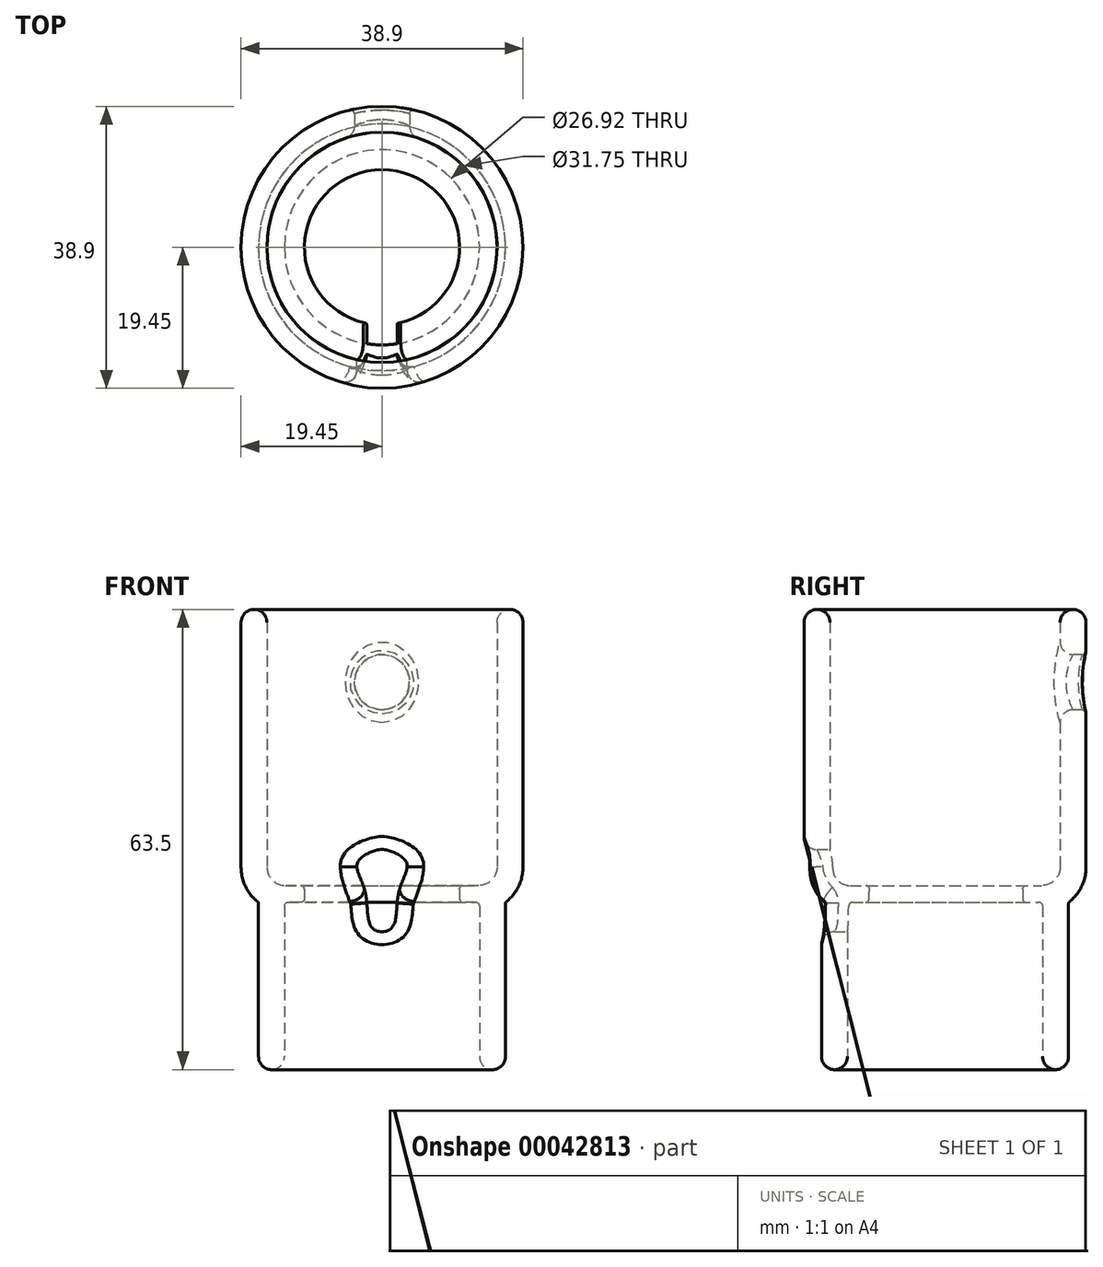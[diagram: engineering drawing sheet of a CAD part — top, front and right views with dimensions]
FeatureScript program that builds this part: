
annotation { "Feature Type Name" : "Feature", "Feature Type Description" : "" }
export const myFeature = defineFeature(function(context is Context, id is Id, definition is map)
    precondition{}
    {
        {
            var Q0;
            Q0=qCreatedBy(makeId("Front.planeOp"),FACE);
            var sketch = newSketch(context, id + "F0", { "sketchPlane" : qUnion([Q0])});
            skLineSegment(sketch, "E0", {"start": v(15.87, 61.71) * mm, "end": v(15.87, 27.94) * mm});
            skLineSegment(sketch, "E1", {"start": v(13.33, 25.4) * mm, "end": v(11.21, 25.4) * mm});
            skLineSegment(sketch, "E2", {"start": v(13.46, 22.57) * mm, "end": v(13.46, 1.79) * mm});
            skPoint(sketch, "E3.visualSharp", {"position": v(15.88, 25.4) * mm});
            skArc(sketch, "E3.filletArc", {"start": v(13.33, 25.4) * mm, "mid": v(15.13, 26.14) * mm, "end": v(15.87, 27.94) * mm});
            skLineSegment(sketch, "E4", {"start": v(0, -28.34) * mm, "end": v(0, 90.61) * mm, "construction": true});
            skCircle(sketch, "E5", {"center": v(0, 53.46) * mm, "radius": 3.81 * mm});
            skPoint(sketch, "E6", {"position": v(0, 61.71) * mm});
            skLineSegment(sketch, "E7.0", {"start": v(17.03, 22.83) * mm, "end": v(17.03, 1.79) * mm});
            skArc(sketch, "E7.1", {"start": v(17.22, 23.22) * mm, "mid": v(18.86, 25.33) * mm, "end": v(19.45, 27.94) * mm});
            skLineSegment(sketch, "E7.2", {"start": v(19.45, 61.71) * mm, "end": v(19.45, 27.94) * mm});
            skArc(sketch, "E8", {"start": v(15.87, 61.71) * mm, "mid": v(17.66, 63.5) * mm, "end": v(19.45, 61.71) * mm});
            skArc(sketch, "E9", {"start": v(13.46, 1.79) * mm, "mid": v(15.25, 0) * mm, "end": v(17.03, 1.79) * mm});
            skPoint(sketch, "E10", {"position": v(15.25, 0) * mm});
            skPoint(sketch, "E11", {"position": v(17.66, 63.5) * mm});
            skLineSegment(sketch, "E12", {"start": v(10.7, 24.9) * mm, "end": v(10.7, 23.58) * mm});
            skLineSegment(sketch, "E13", {"start": v(11.21, 23.07) * mm, "end": v(12.95, 23.07) * mm});
            skPoint(sketch, "E14.visualSharp", {"position": v(10.7, 25.4) * mm});
            skArc(sketch, "E14.filletArc", {"start": v(11.21, 25.4) * mm, "mid": v(10.85, 25.25) * mm, "end": v(10.7, 24.9) * mm});
            skPoint(sketch, "E15.visualSharp", {"position": v(10.7, 23.07) * mm});
            skArc(sketch, "E15.filletArc", {"start": v(10.7, 23.58) * mm, "mid": v(10.85, 23.22) * mm, "end": v(11.21, 23.07) * mm});
            skPoint(sketch, "E16.visualSharp", {"position": v(13.46, 23.07) * mm});
            skArc(sketch, "E16.filletArc", {"start": v(13.46, 22.57) * mm, "mid": v(13.31, 22.93) * mm, "end": v(12.95, 23.07) * mm});
            skPoint(sketch, "E17.visualSharp", {"position": v(17.03, 23.07) * mm});
            skArc(sketch, "E17.filletArc", {"start": v(17.22, 23.22) * mm, "mid": v(17.08, 23.05) * mm, "end": v(17.03, 22.83) * mm});
            skSolve(sketch);
        }
        {
            var Q0;
            Q0=makeQuery(id+"F0.imprint","IMPRINT",FACE,{"disambiguationData":[TD([[makeQuery(id+"F0.imprint","IMPRINT",EDGE,{"derivedFrom":sQuery(id+"F0.wireOp",EDGE,"E0")}),1.0]])]});
            var Q1;
            Q1=sQuery(id+"F0.wireOp",EDGE,"E4");
            revolve(context, id + "F1", {"entities" : qUnion([Q0]), "axis" : qUnion([Q1]), "revolveType" : RevolveType.FULL});
        }
        {
            var Q0;
            Q0=makeQuery(id+"F0.imprint","IMPRINT",FACE,{"disambiguationData":[TD([[makeQuery(id+"F0.imprint","IMPRINT",EDGE,{"derivedFrom":sQuery(id+"F0.wireOp",EDGE,"E5")}),1.0]])]});
            extrude(context, id + "F2", {"entities" : qUnion([Q0]), "operationType" : NewBodyOperationType.REMOVE, "oppositeDirection" : true, "depth" : 38.1 * mm});
        }
        {
            var Q0;
            Q0=makeQuery(id+"F2.boolean.opBoolean","INTERSECT",EDGE,{"derivedFrom":[makeQuery(id+"F1.opRevolve","SWEPT_FACE",FACE,{"disambiguationData":[OSD([sQuery(id+"F0.wireOp",EDGE,"E0")])]}),makeQuery(id+"F2.opExtrude","SWEPT_FACE",FACE,{"disambiguationData":[OSD([sQuery(id+"F0.wireOp",EDGE,"E5")])]})]});
            fillet(context, id + "F3", {"entities" : qUnion([Q0]), "radius" : 1.78 * mm, "tangentPropagation" : true, "allowEdgeOverflow" : false});
        }
        {
            var Q0;
            Q0=makeQuery(id+"F2.boolean.opBoolean","INTERSECT",EDGE,{"derivedFrom":[makeQuery(id+"F1.opRevolve","SWEPT_FACE",FACE,{"disambiguationData":[OSD([sQuery(id+"F0.wireOp",EDGE,"E7.2")])]}),makeQuery(id+"F2.opExtrude","SWEPT_FACE",FACE,{"disambiguationData":[OSD([sQuery(id+"F0.wireOp",EDGE,"E5")])]})]});
            fillet(context, id + "F4", {"entities" : qUnion([Q0]), "radius" : 0.5 * mm, "tangentPropagation" : true, "allowEdgeOverflow" : false});
        }
        {
            var Q0;
            Q0=qCreatedBy(makeId("Front.planeOp"),FACE);
            var sketch = newSketch(context, id + "F5", { "sketchPlane" : qUnion([Q0])});
            skFitSpline(sketch, "E18", {"points": [v(0, 19.02) * mm, v(2.24, 24.15) * mm, v(3.32, 28.68) * mm, v(0, 30.37) * mm], "startDerivative": vector(19.94, 0) * mm, "endDerivative": vector(-9.19, 0) * mm});
            skFitSpline(sketch, "E19.MirrorCS", {"points": [v(0, 19.02) * mm, v(-2.24, 24.15) * mm, v(-3.32, 28.68) * mm, v(0, 30.37) * mm], "startDerivative": vector(-19.94, 0) * mm, "endDerivative": vector(9.19, 0) * mm});
            skSolve(sketch);
        }
        {
            var Q0;
            Q0 = qSketchRegion(id + "F5", true);
            extrude(context, id + "F6", {"entities" : qUnion([Q0]), "depth" : 50.8 * mm});
        }
        {
            var Q0;
            Q0=makeQuery(id+"F6.opExtrude","SWEPT_BODY",BODY,{"disambiguationData":[OSD([sQuery(id+"F5.wireOp",EDGE,"E18"),sQuery(id+"F5.wireOp",EDGE,"E19.MirrorCS")])]});
            var Q1;
            Q1=makeQuery(id+"F1.opRevolve","SWEPT_BODY",BODY,{"disambiguationData":[OSD([sQuery(id+"F0.wireOp",EDGE,"E0"),sQuery(id+"F0.wireOp",EDGE,"E1"),sQuery(id+"F0.wireOp",EDGE,"E2"),sQuery(id+"F0.wireOp",EDGE,"665b7fc8-37b9-4214-9120-500ffdb07fa3.filletArc"),sQuery(id+"F0.wireOp",EDGE,"E3.filletArc"),sQuery(id+"F0.wireOp",EDGE,"E7.0"),sQuery(id+"F0.wireOp",EDGE,"E7.1"),sQuery(id+"F0.wireOp",EDGE,"E7.2"),sQuery(id+"F0.wireOp",EDGE,"E8"),sQuery(id+"F0.wireOp",EDGE,"E9")])]});
            booleanBodies(context, id + "F7", {"operationType" : BooleanOperationType.SUBTRACTION, "tools" : qUnion([Q0]), "targets" : qUnion([Q1])});
        }
        {
            var Q0;
            {var subQ0=sQuery(id+"F5.wireOp",EDGE,"E19.MirrorCS");var subQ1=sQuery(id+"F5.wireOp",EDGE,"E18");var subQ3=makeQuery(id+"F6.opExtrude","SWEPT_FACE",FACE,{"disambiguationData":[OSD([subQ1])]});var subQ4=makeQuery(id+"Fw3jHcx6r2MQuvf_2.opPattern","COPY",FACE,{"derivedFrom":subQ3,"instanceName":"1"});Q0=makeQuery(id+"F7.opBoolean","INTERSECT",EDGE,{"derivedFrom":[makeQuery(id+"F1.opRevolve","SWEPT_FACE",FACE,{"disambiguationData":[OSD([sQuery(id+"F0.wireOp",EDGE,"E7.1")])]}),makeQuery(id+"Fw3jHcx6r2MQuvf_2.boolean.opBoolean","SPLIT",FACE,{"disambiguationData":[TD([makeQuery(id+"Fw3jHcx6r2MQuvf_2.opPattern","COPY",FACE,{"derivedFrom":makeQuery(id+"F6.opExtrude","CAP_FACE",FACE,{"disambiguationData":[OSD([subQ1,subQ0])],"isStart":false}),"instanceName":"1"})])],"derivedFrom":subQ4})]});}
            var Q1;
            {var subQ0=sQuery(id+"F5.wireOp",EDGE,"E19.MirrorCS");var subQ1=sQuery(id+"F5.wireOp",EDGE,"E18");var subQ3=makeQuery(id+"F6.opExtrude","SWEPT_FACE",FACE,{"disambiguationData":[OSD([subQ1])]});var subQ4=makeQuery(id+"Fw3jHcx6r2MQuvf_2.opPattern","COPY",FACE,{"derivedFrom":subQ3,"instanceName":"1"});Q1=makeQuery(id+"F7.opBoolean","INTERSECT",EDGE,{"derivedFrom":[makeQuery(id+"F1.opRevolve","SWEPT_FACE",FACE,{"disambiguationData":[OSD([sQuery(id+"F0.wireOp",EDGE,"E7.0")])]}),makeQuery(id+"Fw3jHcx6r2MQuvf_2.boolean.opBoolean","SPLIT",FACE,{"disambiguationData":[TD([makeQuery(id+"Fw3jHcx6r2MQuvf_2.opPattern","COPY",FACE,{"derivedFrom":makeQuery(id+"F6.opExtrude","CAP_FACE",FACE,{"disambiguationData":[OSD([subQ1,subQ0])],"isStart":false}),"instanceName":"1"})])],"derivedFrom":subQ4})]});}
            var Q2;
            {var subQ0=sQuery(id+"F5.wireOp",EDGE,"E19.MirrorCS");var subQ1=sQuery(id+"F5.wireOp",EDGE,"E18");var subQ2=makeQuery(id+"F6.opExtrude","SWEPT_FACE",FACE,{"disambiguationData":[OSD([subQ0])]});var subQ4=makeQuery(id+"Fw3jHcx6r2MQuvf_2.opPattern","COPY",FACE,{"derivedFrom":subQ2,"instanceName":"1"});Q2=makeQuery(id+"F7.opBoolean","INTERSECT",EDGE,{"derivedFrom":[makeQuery(id+"F1.opRevolve","SWEPT_FACE",FACE,{"disambiguationData":[OSD([sQuery(id+"F0.wireOp",EDGE,"E7.0")])]}),makeQuery(id+"Fw3jHcx6r2MQuvf_2.boolean.opBoolean","SPLIT",FACE,{"disambiguationData":[TD([makeQuery(id+"Fw3jHcx6r2MQuvf_2.opPattern","COPY",FACE,{"derivedFrom":makeQuery(id+"F6.opExtrude","CAP_FACE",FACE,{"disambiguationData":[OSD([subQ1,subQ0])],"isStart":false}),"instanceName":"1"})])],"derivedFrom":subQ4})]});}
            var Q3;
            {var subQ0=sQuery(id+"F5.wireOp",EDGE,"E18");var subQ1=makeQuery(id+"F6.opExtrude","SWEPT_FACE",FACE,{"disambiguationData":[OSD([subQ0])]});var subQ2=sQuery(id+"F5.wireOp",EDGE,"E19.MirrorCS");Q3=makeQuery(id+"F7.opBoolean","INTERSECT",EDGE,{"derivedFrom":[makeQuery(id+"F1.opRevolve","SWEPT_FACE",FACE,{"disambiguationData":[OSD([sQuery(id+"F0.wireOp",EDGE,"E7.2")])]}),makeQuery(id+"Fw3jHcx6r2MQuvf_2.boolean.opBoolean","SPLIT",FACE,{"disambiguationData":[TD([makeQuery(id+"F6.opExtrude","CAP_FACE",FACE,{"disambiguationData":[OSD([subQ0,subQ2])],"isStart":false})])],"derivedFrom":subQ1})]});}
            var Q4;
            {var subQ0=sQuery(id+"F5.wireOp",EDGE,"E18");var subQ2=sQuery(id+"F5.wireOp",EDGE,"E19.MirrorCS");var subQ3=makeQuery(id+"F6.opExtrude","SWEPT_FACE",FACE,{"disambiguationData":[OSD([subQ2])]});Q4=makeQuery(id+"F7.opBoolean","INTERSECT",EDGE,{"derivedFrom":[makeQuery(id+"F1.opRevolve","SWEPT_FACE",FACE,{"disambiguationData":[OSD([sQuery(id+"F0.wireOp",EDGE,"E7.0")])]}),makeQuery(id+"Fw3jHcx6r2MQuvf_2.boolean.opBoolean","SPLIT",FACE,{"disambiguationData":[TD([makeQuery(id+"F6.opExtrude","CAP_FACE",FACE,{"disambiguationData":[OSD([subQ0,subQ2])],"isStart":false})])],"derivedFrom":subQ3})]});}
            var Q5;
            {var subQ0=sQuery(id+"F5.wireOp",EDGE,"E19.MirrorCS");var subQ2=sQuery(id+"F5.wireOp",EDGE,"E18");var subQ3=makeQuery(id+"F6.opExtrude","SWEPT_FACE",FACE,{"disambiguationData":[OSD([subQ2])]});var subQ4=makeQuery(id+"Fw3jHcx6r2MQuvf_2.opPattern","COPY",FACE,{"derivedFrom":subQ3,"instanceName":"2"});Q5=makeQuery(id+"F7.opBoolean","INTERSECT",EDGE,{"derivedFrom":[makeQuery(id+"F1.opRevolve","SWEPT_FACE",FACE,{"disambiguationData":[OSD([sQuery(id+"F0.wireOp",EDGE,"E7.0")])]}),makeQuery(id+"Fw3jHcx6r2MQuvf_2.boolean.opBoolean","SPLIT",FACE,{"disambiguationData":[TD([makeQuery(id+"Fw3jHcx6r2MQuvf_2.opPattern","COPY",FACE,{"derivedFrom":makeQuery(id+"F6.opExtrude","CAP_FACE",FACE,{"disambiguationData":[OSD([subQ2,subQ0])],"isStart":false}),"instanceName":"2"})])],"derivedFrom":subQ4})]});}
            var Q6;
            {var subQ0=sQuery(id+"F5.wireOp",EDGE,"E19.MirrorCS");var subQ2=sQuery(id+"F5.wireOp",EDGE,"E18");var subQ3=makeQuery(id+"F6.opExtrude","SWEPT_FACE",FACE,{"disambiguationData":[OSD([subQ2])]});var subQ4=makeQuery(id+"Fw3jHcx6r2MQuvf_2.opPattern","COPY",FACE,{"derivedFrom":subQ3,"instanceName":"2"});Q6=makeQuery(id+"F7.opBoolean","INTERSECT",EDGE,{"derivedFrom":[makeQuery(id+"F1.opRevolve","SWEPT_FACE",FACE,{"disambiguationData":[OSD([sQuery(id+"F0.wireOp",EDGE,"E7.1")])]}),makeQuery(id+"Fw3jHcx6r2MQuvf_2.boolean.opBoolean","SPLIT",FACE,{"disambiguationData":[TD([makeQuery(id+"Fw3jHcx6r2MQuvf_2.opPattern","COPY",FACE,{"derivedFrom":makeQuery(id+"F6.opExtrude","CAP_FACE",FACE,{"disambiguationData":[OSD([subQ2,subQ0])],"isStart":false}),"instanceName":"2"})])],"derivedFrom":subQ4})]});}
            var Q7;
            {var subQ0=sQuery(id+"F5.wireOp",EDGE,"E18");var subQ2=sQuery(id+"F5.wireOp",EDGE,"E19.MirrorCS");var subQ3=makeQuery(id+"F6.opExtrude","SWEPT_FACE",FACE,{"disambiguationData":[OSD([subQ2])]});Q7=makeQuery(id+"F7.opBoolean","INTERSECT",EDGE,{"derivedFrom":[makeQuery(id+"F1.opRevolve","SWEPT_FACE",FACE,{"disambiguationData":[OSD([sQuery(id+"F0.wireOp",EDGE,"E7.2")])]}),makeQuery(id+"Fw3jHcx6r2MQuvf_2.boolean.opBoolean","SPLIT",FACE,{"disambiguationData":[TD([makeQuery(id+"F6.opExtrude","CAP_FACE",FACE,{"disambiguationData":[OSD([subQ0,subQ2])],"isStart":true})])],"derivedFrom":subQ3})]});}
            var Q8;
            {var subQ0=sQuery(id+"F5.wireOp",EDGE,"E18");var subQ2=sQuery(id+"F5.wireOp",EDGE,"E19.MirrorCS");var subQ3=makeQuery(id+"F6.opExtrude","SWEPT_FACE",FACE,{"disambiguationData":[OSD([subQ2])]});Q8=makeQuery(id+"F7.opBoolean","INTERSECT",EDGE,{"derivedFrom":[makeQuery(id+"F1.opRevolve","SWEPT_FACE",FACE,{"disambiguationData":[OSD([sQuery(id+"F0.wireOp",EDGE,"E7.0")])]}),makeQuery(id+"Fw3jHcx6r2MQuvf_2.boolean.opBoolean","SPLIT",FACE,{"disambiguationData":[TD([makeQuery(id+"F6.opExtrude","CAP_FACE",FACE,{"disambiguationData":[OSD([subQ0,subQ2])],"isStart":true})])],"derivedFrom":subQ3})]});}
            var Q9;
            {var subQ0=sQuery(id+"F5.wireOp",EDGE,"E18");var subQ2=sQuery(id+"F5.wireOp",EDGE,"E19.MirrorCS");var subQ3=makeQuery(id+"F6.opExtrude","SWEPT_FACE",FACE,{"disambiguationData":[OSD([subQ2])]});Q9=makeQuery(id+"F7.opBoolean","INTERSECT",EDGE,{"derivedFrom":[makeQuery(id+"F1.opRevolve","SWEPT_FACE",FACE,{"disambiguationData":[OSD([sQuery(id+"F0.wireOp",EDGE,"E7.1")])]}),makeQuery(id+"Fw3jHcx6r2MQuvf_2.boolean.opBoolean","SPLIT",FACE,{"disambiguationData":[TD([makeQuery(id+"F6.opExtrude","CAP_FACE",FACE,{"disambiguationData":[OSD([subQ0,subQ2])],"isStart":true})])],"derivedFrom":subQ3})]});}
            var Q10;
            {var subQ0=sQuery(id+"F5.wireOp",EDGE,"E18");var subQ2=sQuery(id+"F5.wireOp",EDGE,"E19.MirrorCS");var subQ3=makeQuery(id+"F6.opExtrude","SWEPT_FACE",FACE,{"disambiguationData":[OSD([subQ2])]});var subQ4=makeQuery(id+"Fw3jHcx6r2MQuvf_2.opPattern","COPY",FACE,{"derivedFrom":subQ3,"instanceName":"1"});Q10=makeQuery(id+"F7.opBoolean","INTERSECT",EDGE,{"derivedFrom":[makeQuery(id+"F1.opRevolve","SWEPT_FACE",FACE,{"disambiguationData":[OSD([sQuery(id+"F0.wireOp",EDGE,"E7.1")])]}),makeQuery(id+"Fw3jHcx6r2MQuvf_2.boolean.opBoolean","SPLIT",FACE,{"disambiguationData":[TD([makeQuery(id+"Fw3jHcx6r2MQuvf_2.opPattern","COPY",FACE,{"derivedFrom":makeQuery(id+"F6.opExtrude","CAP_FACE",FACE,{"disambiguationData":[OSD([subQ0,subQ2])],"isStart":true}),"instanceName":"1"})])],"derivedFrom":subQ4})]});}
            var Q11;
            {var subQ0=sQuery(id+"F5.wireOp",EDGE,"E18");var subQ2=sQuery(id+"F5.wireOp",EDGE,"E19.MirrorCS");var subQ3=makeQuery(id+"F6.opExtrude","SWEPT_FACE",FACE,{"disambiguationData":[OSD([subQ2])]});var subQ4=makeQuery(id+"Fw3jHcx6r2MQuvf_2.opPattern","COPY",FACE,{"derivedFrom":subQ3,"instanceName":"1"});Q11=makeQuery(id+"F7.opBoolean","INTERSECT",EDGE,{"derivedFrom":[makeQuery(id+"F1.opRevolve","SWEPT_FACE",FACE,{"disambiguationData":[OSD([sQuery(id+"F0.wireOp",EDGE,"E7.2")])]}),makeQuery(id+"Fw3jHcx6r2MQuvf_2.boolean.opBoolean","SPLIT",FACE,{"disambiguationData":[TD([makeQuery(id+"Fw3jHcx6r2MQuvf_2.opPattern","COPY",FACE,{"derivedFrom":makeQuery(id+"F6.opExtrude","CAP_FACE",FACE,{"disambiguationData":[OSD([subQ0,subQ2])],"isStart":true}),"instanceName":"1"})])],"derivedFrom":subQ4})]});}
            var Q12;
            {var subQ0=sQuery(id+"F5.wireOp",EDGE,"E18");var subQ2=sQuery(id+"F5.wireOp",EDGE,"E19.MirrorCS");var subQ3=makeQuery(id+"F6.opExtrude","SWEPT_FACE",FACE,{"disambiguationData":[OSD([subQ2])]});var subQ4=makeQuery(id+"Fw3jHcx6r2MQuvf_2.opPattern","COPY",FACE,{"derivedFrom":subQ3,"instanceName":"1"});Q12=makeQuery(id+"F7.opBoolean","INTERSECT",EDGE,{"derivedFrom":[makeQuery(id+"F1.opRevolve","SWEPT_FACE",FACE,{"disambiguationData":[OSD([sQuery(id+"F0.wireOp",EDGE,"E7.0")])]}),makeQuery(id+"Fw3jHcx6r2MQuvf_2.boolean.opBoolean","SPLIT",FACE,{"disambiguationData":[TD([makeQuery(id+"Fw3jHcx6r2MQuvf_2.opPattern","COPY",FACE,{"derivedFrom":makeQuery(id+"F6.opExtrude","CAP_FACE",FACE,{"disambiguationData":[OSD([subQ0,subQ2])],"isStart":true}),"instanceName":"1"})])],"derivedFrom":subQ4})]});}
            var Q13;
            {var subQ0=sQuery(id+"F5.wireOp",EDGE,"E19.MirrorCS");var subQ1=makeQuery(id+"F6.opExtrude","SWEPT_FACE",FACE,{"disambiguationData":[OSD([subQ0])]});var subQ2=sQuery(id+"F5.wireOp",EDGE,"E18");var subQ4=makeQuery(id+"Fw3jHcx6r2MQuvf_2.opPattern","COPY",FACE,{"derivedFrom":subQ1,"instanceName":"2"});Q13=makeQuery(id+"F7.opBoolean","INTERSECT",EDGE,{"derivedFrom":[makeQuery(id+"F1.opRevolve","SWEPT_FACE",FACE,{"disambiguationData":[OSD([sQuery(id+"F0.wireOp",EDGE,"E7.2")])]}),makeQuery(id+"Fw3jHcx6r2MQuvf_2.boolean.opBoolean","SPLIT",FACE,{"disambiguationData":[TD([makeQuery(id+"Fw3jHcx6r2MQuvf_2.opPattern","COPY",FACE,{"derivedFrom":makeQuery(id+"F6.opExtrude","CAP_FACE",FACE,{"disambiguationData":[OSD([subQ2,subQ0])],"isStart":true}),"instanceName":"2"})])],"derivedFrom":subQ4})]});}
            var Q14;
            {var subQ0=sQuery(id+"F5.wireOp",EDGE,"E19.MirrorCS");var subQ1=makeQuery(id+"F6.opExtrude","SWEPT_FACE",FACE,{"disambiguationData":[OSD([subQ0])]});var subQ2=sQuery(id+"F5.wireOp",EDGE,"E18");var subQ4=makeQuery(id+"Fw3jHcx6r2MQuvf_2.opPattern","COPY",FACE,{"derivedFrom":subQ1,"instanceName":"2"});Q14=makeQuery(id+"F7.opBoolean","INTERSECT",EDGE,{"derivedFrom":[makeQuery(id+"F1.opRevolve","SWEPT_FACE",FACE,{"disambiguationData":[OSD([sQuery(id+"F0.wireOp",EDGE,"E7.1")])]}),makeQuery(id+"Fw3jHcx6r2MQuvf_2.boolean.opBoolean","SPLIT",FACE,{"disambiguationData":[TD([makeQuery(id+"Fw3jHcx6r2MQuvf_2.opPattern","COPY",FACE,{"derivedFrom":makeQuery(id+"F6.opExtrude","CAP_FACE",FACE,{"disambiguationData":[OSD([subQ2,subQ0])],"isStart":true}),"instanceName":"2"})])],"derivedFrom":subQ4})]});}
            var Q15;
            {var subQ0=sQuery(id+"F5.wireOp",EDGE,"E19.MirrorCS");var subQ1=makeQuery(id+"F6.opExtrude","SWEPT_FACE",FACE,{"disambiguationData":[OSD([subQ0])]});var subQ2=sQuery(id+"F5.wireOp",EDGE,"E18");var subQ4=makeQuery(id+"Fw3jHcx6r2MQuvf_2.opPattern","COPY",FACE,{"derivedFrom":subQ1,"instanceName":"2"});Q15=makeQuery(id+"F7.opBoolean","INTERSECT",EDGE,{"derivedFrom":[makeQuery(id+"F1.opRevolve","SWEPT_FACE",FACE,{"disambiguationData":[OSD([sQuery(id+"F0.wireOp",EDGE,"E7.0")])]}),makeQuery(id+"Fw3jHcx6r2MQuvf_2.boolean.opBoolean","SPLIT",FACE,{"disambiguationData":[TD([makeQuery(id+"Fw3jHcx6r2MQuvf_2.opPattern","COPY",FACE,{"derivedFrom":makeQuery(id+"F6.opExtrude","CAP_FACE",FACE,{"disambiguationData":[OSD([subQ2,subQ0])],"isStart":true}),"instanceName":"2"})])],"derivedFrom":subQ4})]});}
            fillet(context, id + "F8", {"entities" : qUnion([Q0, Q1, Q2, Q3, Q4, Q5, Q6, Q7, Q8, Q9, Q10, Q11, Q12, Q13, Q14, Q15]), "radius" : 1.78 * mm, "tangentPropagation" : true, "allowEdgeOverflow" : false});
        }
    });
